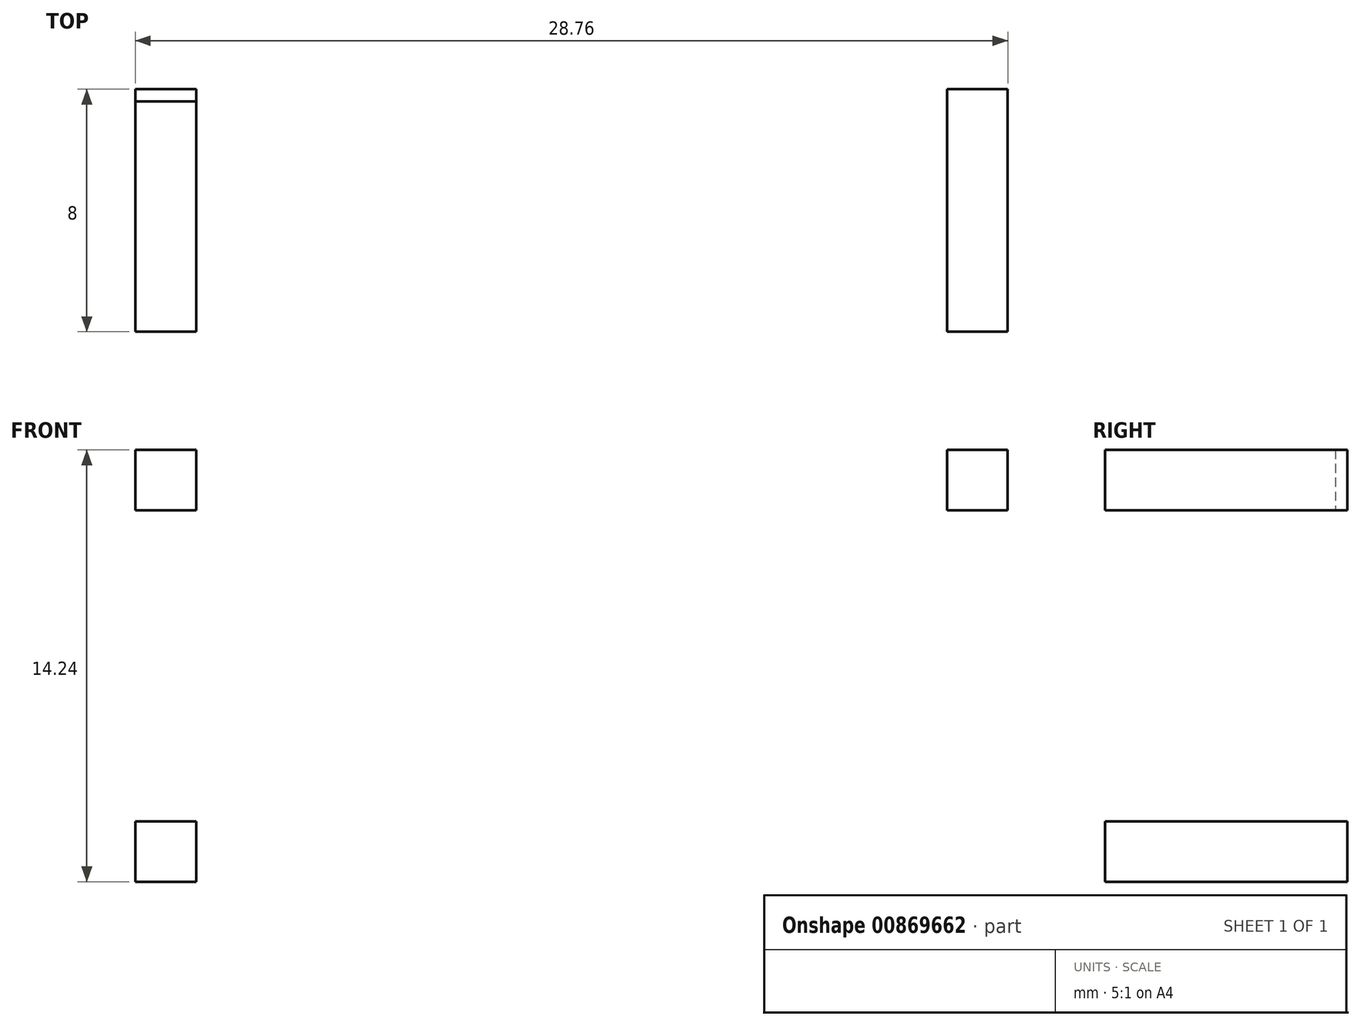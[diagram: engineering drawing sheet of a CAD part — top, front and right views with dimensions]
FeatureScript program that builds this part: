
annotation { "Feature Type Name" : "Feature", "Feature Type Description" : "" }
export const myFeature = defineFeature(function(context is Context, id is Id, definition is map)
    precondition{}
    {
        {
            var Q0;
            Q0=qCreatedBy(makeId("Front.planeOp"),FACE);
            var sketch = newSketch(context, id + "F0", { "sketchPlane" : qUnion([Q0])});
            skLineSegment(sketch, "E0.bottom", {"start": v(14.38, 7.12) * mm, "end": v(-14.38, 7.12) * mm});
            skLineSegment(sketch, "E0.top", {"start": v(14.38, -7.12) * mm, "end": v(-14.38, -7.12) * mm});
            skLineSegment(sketch, "E0.left", {"start": v(14.38, 7.12) * mm, "end": v(14.38, -7.12) * mm});
            skLineSegment(sketch, "E0.right", {"start": v(-14.38, 7.12) * mm, "end": v(-14.38, -7.12) * mm});
            skPoint(sketch, "E0.middle", {"position": v(0, 0) * mm});
            skLineSegment(sketch, "E1.bottom", {"start": v(-14.38, 7.12) * mm, "end": v(-12.38, 7.12) * mm});
            skLineSegment(sketch, "E1.top", {"start": v(-14.38, 5.12) * mm, "end": v(-12.38, 5.12) * mm});
            skLineSegment(sketch, "E1.left", {"start": v(-14.38, 7.12) * mm, "end": v(-14.38, 5.12) * mm});
            skLineSegment(sketch, "E1.right", {"start": v(-12.38, 7.12) * mm, "end": v(-12.38, 5.12) * mm});
            skLineSegment(sketch, "E2.MirrorCS", {"start": v(12.38, 7.12) * mm, "end": v(12.38, 5.12) * mm});
            skLineSegment(sketch, "E3.MirrorCS", {"start": v(14.38, 7.12) * mm, "end": v(12.38, 7.12) * mm});
            skLineSegment(sketch, "E4.MirrorCS", {"start": v(14.38, 7.12) * mm, "end": v(14.38, 5.12) * mm});
            skLineSegment(sketch, "E5.MirrorCS", {"start": v(14.38, 5.12) * mm, "end": v(12.38, 5.12) * mm});
            skLineSegment(sketch, "E6.MirrorCS", {"start": v(-14.38, -5.12) * mm, "end": v(-12.38, -5.12) * mm});
            skLineSegment(sketch, "E7.MirrorCS", {"start": v(-12.38, -7.12) * mm, "end": v(-12.38, -5.12) * mm});
            skLineSegment(sketch, "E8.MirrorCS", {"start": v(-14.38, -7.12) * mm, "end": v(-12.38, -7.12) * mm});
            skLineSegment(sketch, "E9.MirrorCS", {"start": v(14.38, -7.12) * mm, "end": v(12.38, -7.12) * mm});
            skLineSegment(sketch, "E10.MirrorCS", {"start": v(14.38, -5.12) * mm, "end": v(12.38, -5.12) * mm});
            skLineSegment(sketch, "E11.MirrorCS", {"start": v(12.38, -7.12) * mm, "end": v(12.38, -5.12) * mm});
            skLineSegment(sketch, "E12.MirrorCS", {"start": v(14.38, -7.12) * mm, "end": v(14.38, -5.12) * mm});
            skSolve(sketch);
        }
        {
            var Q0;
            Q0=makeQuery(id+"F0.imprint","IMPRINT",FACE,{"disambiguationData":[TD([[makeQuery(id+"F0.imprint","IMPRINT",EDGE,{"derivedFrom":sQuery(id+"F0.wireOp",EDGE,"E0.bottom")}),1.0]])]});
            extrude(context, id + "F1", {"entities" : qUnion([Q0]), "depth" : .4 * mm, "offsetDistance" : 25 * mm});
        }
        {
            var Q0;
            Q0=makeQuery(id+"F0.imprint","IMPRINT",FACE,{"disambiguationData":[TD([[makeQuery(id+"F0.imprint","IMPRINT",EDGE,{"derivedFrom":sQuery(id+"F0.wireOp",EDGE,"E1.bottom")}),-1.0]])]});
            var Q1;
            {var subQ2=sQuery(id+"F0.wireOp",EDGE,"E6.MirrorCS");Q1=makeQuery(id+"F0.imprint","IMPRINT",FACE,{"disambiguationData":[TD([[makeQuery(id+"F0.imprint","IMPRINT",EDGE,{"derivedFrom":subQ2}),-1.0]])]});}
            var Q2;
            Q2=makeQuery(id+"F0.imprint","IMPRINT",FACE,{"disambiguationData":[TD([[makeQuery(id+"F0.imprint","IMPRINT",EDGE,{"derivedFrom":sQuery(id+"F0.wireOp",EDGE,"E9.MirrorCS")}),-1.0]])]});
            var Q3;
            Q3=makeQuery(id+"F0.imprint","IMPRINT",FACE,{"disambiguationData":[TD([[makeQuery(id+"F0.imprint","IMPRINT",EDGE,{"derivedFrom":sQuery(id+"F0.wireOp",EDGE,"E2.MirrorCS")}),1.0]])]});
            extrude(context, id + "F2", {"entities" : qUnion([Q0, Q1, Q2, Q3]), "operationType" : NewBodyOperationType.ADD, "depth" : 8 * mm, "offsetDistance" : 25 * mm});
        }
    });
